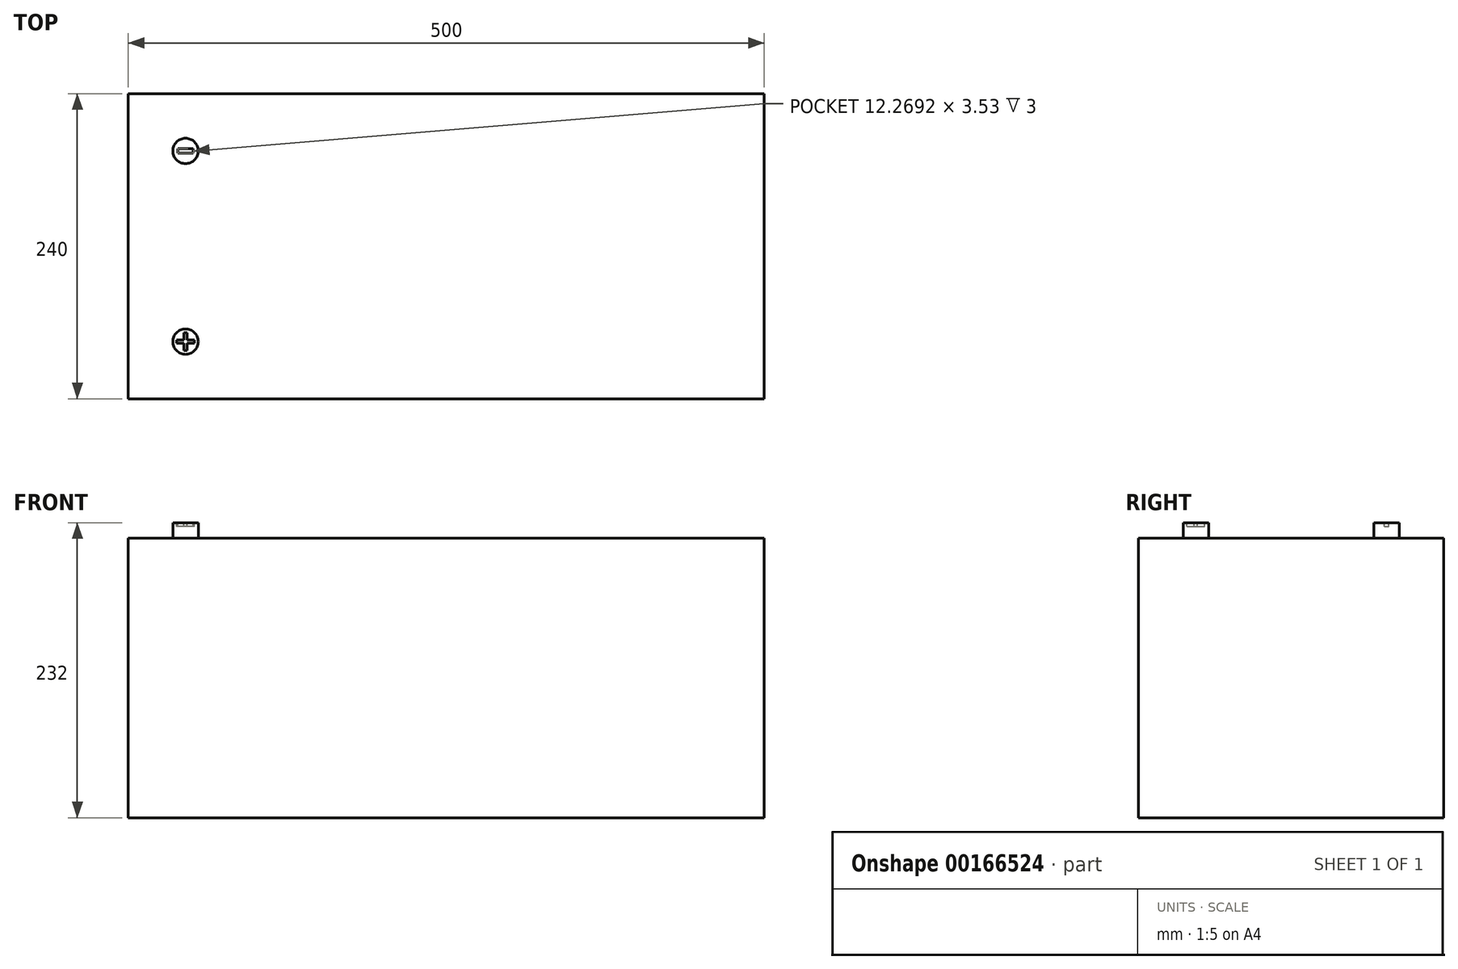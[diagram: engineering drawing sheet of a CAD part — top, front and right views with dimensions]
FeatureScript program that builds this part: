
annotation { "Feature Type Name" : "Feature", "Feature Type Description" : "" }
export const myFeature = defineFeature(function(context is Context, id is Id, definition is map)
    precondition{}
    {
        {
            var Q0;
            Q0=qCreatedBy(makeId("Top.planeOp"),FACE);
            var sketch = newSketch(context, id + "F0", { "sketchPlane" : qUnion([Q0])});
            skLineSegment(sketch, "E0.bottom", {"start": v(251.3, -120) * mm, "end": v(-248.7, -120) * mm});
            skLineSegment(sketch, "E0.top", {"start": v(251.3, 120) * mm, "end": v(-248.7, 120) * mm});
            skLineSegment(sketch, "E0.left", {"start": v(251.3, -120) * mm, "end": v(251.3, 120) * mm});
            skLineSegment(sketch, "E0.right", {"start": v(-248.7, -120) * mm, "end": v(-248.7, 120) * mm});
            skPoint(sketch, "E0.middle", {"position": v(1.3, 0) * mm});
            skSolve(sketch);
        }
        {
            var Q0;
            Q0=makeQuery(id+"F0.imprint","IMPRINT",FACE,{"disambiguationData":[TD([[makeQuery(id+"F0.imprint","IMPRINT",EDGE,{"derivedFrom":sQuery(id+"F0.wireOp",EDGE,"E0.bottom")}),-1.0]])]});
            extrude(context, id + "F1", {"entities" : qUnion([Q0]), "depth" : 220 * mm});
        }
        {
            var Q0;
            Q0=makeQuery(id+"F1.opExtrude","CAP_FACE",FACE,{"disambiguationData":[OSD([sQuery(id+"F0.wireOp",EDGE,"E0.bottom"),sQuery(id+"F0.wireOp",EDGE,"E0.top"),sQuery(id+"F0.wireOp",EDGE,"E0.left"),sQuery(id+"F0.wireOp",EDGE,"E0.right")])],"isStart":false});
            var sketch = newSketch(context, id + "F2", { "sketchPlane" : qUnion([Q0])});
            skLineSegment(sketch, "E1", {"start": v(-248.7, 75) * mm, "end": v(-203.7, 75) * mm, "construction": true});
            skLineSegment(sketch, "E2", {"start": v(-203.7, 75) * mm, "end": v(-203.7, 120) * mm, "construction": true});
            skLineSegment(sketch, "E3", {"start": v(-203.7, -120) * mm, "end": v(-203.7, -75) * mm, "construction": true});
            skLineSegment(sketch, "E4", {"start": v(-203.7, -75) * mm, "end": v(-248.7, -75) * mm, "construction": true});
            skCircle(sketch, "E5", {"center": v(-203.7, 75) * mm, "radius": 10 * mm});
            skCircle(sketch, "E6", {"center": v(-203.7, -75) * mm, "radius": 10 * mm});
            skSolve(sketch);
        }
        {
            var Q0;
            Q0=makeQuery(id+"F2.imprint","IMPRINT",FACE,{"disambiguationData":[TD([[makeQuery(id+"F2.imprint","IMPRINT",EDGE,{"derivedFrom":sQuery(id+"F2.wireOp",EDGE,"E5")}),1.0]])]});
            var Q1;
            Q1=makeQuery(id+"F2.imprint","IMPRINT",FACE,{"disambiguationData":[TD([[makeQuery(id+"F2.imprint","IMPRINT",EDGE,{"derivedFrom":sQuery(id+"F2.wireOp",EDGE,"E6")}),1.0]])]});
            extrude(context, id + "F3", {"entities" : qUnion([Q0, Q1]), "operationType" : NewBodyOperationType.ADD, "depth" : 12 * mm});
        }
        {
            var Q0;
            Q0=makeQuery(id+"F3.opExtrude","CAP_FACE",FACE,{"disambiguationData":[OSD([sQuery(id+"F2.wireOp",EDGE,"E5")])],"isStart":false});
            var sketch = newSketch(context, id + "F4", { "sketchPlane" : qUnion([Q0])});
            skLineSegment(sketch, "E7", {"start": v(-203.82, 85) * mm, "end": v(-203.7, 75) * mm, "construction": true});
            skLineSegment(sketch, "E8", {"start": v(-203.7, 75) * mm, "end": v(-203.7, 65) * mm, "construction": true});
            skLineSegment(sketch, "E9", {"start": v(-203.7, 75) * mm, "end": v(-193.7, 75.12) * mm, "construction": true});
            skLineSegment(sketch, "E10", {"start": v(-203.7, 75) * mm, "end": v(-213.7, 74.88) * mm, "construction": true});
            skLineSegment(sketch, "E11.bottom", {"start": v(-197.57, 73.24) * mm, "end": v(-209.83, 73.24) * mm});
            skLineSegment(sketch, "E11.top", {"start": v(-197.57, 76.77) * mm, "end": v(-209.83, 76.77) * mm});
            skLineSegment(sketch, "E11.left", {"start": v(-197.57, 73.24) * mm, "end": v(-197.57, 76.77) * mm});
            skLineSegment(sketch, "E11.right", {"start": v(-209.83, 73.24) * mm, "end": v(-209.83, 76.77) * mm});
            skPoint(sketch, "E11.middle", {"position": v(-203.7, 75) * mm});
            skPoint(sketch, "E12.middle", {"position": v(-203.7, -75) * mm});
            skLineSegment(sketch, "E13.bottom", {"start": v(-196.7, -76.25) * mm, "end": v(-210.7, -76.25) * mm});
            skLineSegment(sketch, "E13.top", {"start": v(-196.7, -73.75) * mm, "end": v(-210.7, -73.75) * mm});
            skLineSegment(sketch, "E13.left", {"start": v(-196.7, -76.25) * mm, "end": v(-196.7, -73.75) * mm});
            skLineSegment(sketch, "E13.right", {"start": v(-210.7, -76.25) * mm, "end": v(-210.7, -73.75) * mm});
            skLineSegment(sketch, "E14.bottom", {"start": v(-202.45, -82) * mm, "end": v(-204.95, -82) * mm});
            skLineSegment(sketch, "E14.top", {"start": v(-202.45, -68) * mm, "end": v(-204.95, -68) * mm});
            skLineSegment(sketch, "E14.left", {"start": v(-202.45, -82) * mm, "end": v(-202.45, -68) * mm});
            skLineSegment(sketch, "E14.right", {"start": v(-204.95, -82) * mm, "end": v(-204.95, -68) * mm});
            skSolve(sketch);
        }
        {
            var Q0;
            Q0=makeQuery(id+"F4.imprint","IMPRINT",FACE,{"disambiguationData":[TD([[makeQuery(id+"F4.imprint","IMPRINT",EDGE,{"derivedFrom":sQuery(id+"F4.wireOp",EDGE,"E11.bottom")}),-1.0]])]});
            var Q1;
            {var subQ0=sQuery(id+"F4.wireOp",EDGE,"E13.right");Q1=makeQuery(id+"F4.imprint","IMPRINT",FACE,{"disambiguationData":[TD([[makeQuery(id+"F4.imprint","IMPRINT",EDGE,{"derivedFrom":subQ0}),-1.0]])]});}
            var Q2;
            {var subQ0=sQuery(id+"F4.wireOp",EDGE,"E14.left");var subQ1=sQuery(id+"F4.wireOp",EDGE,"E13.bottom");var subQ2=makeQuery(id+"F4.imprint","INTERSECT",VERTEX,{"derivedFrom":[subQ1,subQ0]});Q2=makeQuery(id+"F4.imprint","IMPRINT",FACE,{"disambiguationData":[TD([[makeQuery(id+"F4.imprint","IMPRINT",EDGE,{"disambiguationData":[TD([[subQ2,-1.0]])],"derivedFrom":subQ1}),-1.0]])]});}
            var Q3;
            {var subQ0=sQuery(id+"F4.wireOp",EDGE,"E13.left");Q3=makeQuery(id+"F4.imprint","IMPRINT",FACE,{"disambiguationData":[TD([[makeQuery(id+"F4.imprint","IMPRINT",EDGE,{"derivedFrom":subQ0}),1.0]])]});}
            var Q4;
            {var subQ5=sQuery(id+"F4.wireOp",EDGE,"E14.top");Q4=makeQuery(id+"F4.imprint","IMPRINT",FACE,{"disambiguationData":[TD([[makeQuery(id+"F4.imprint","IMPRINT",EDGE,{"derivedFrom":subQ5}),1.0]])]});}
            var Q5;
            {var subQ5=sQuery(id+"F4.wireOp",EDGE,"E14.bottom");Q5=makeQuery(id+"F4.imprint","IMPRINT",FACE,{"disambiguationData":[TD([[makeQuery(id+"F4.imprint","IMPRINT",EDGE,{"derivedFrom":subQ5}),-1.0]])]});}
            extrude(context, id + "F5", {"entities" : qUnion([Q0, Q1, Q2, Q3, Q4, Q5]), "operationType" : NewBodyOperationType.REMOVE, "oppositeDirection" : true, "depth" : 3 * mm});
        }
    });
